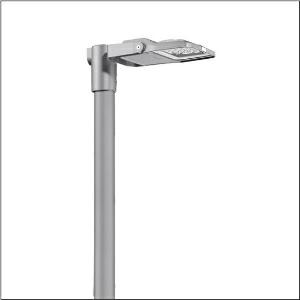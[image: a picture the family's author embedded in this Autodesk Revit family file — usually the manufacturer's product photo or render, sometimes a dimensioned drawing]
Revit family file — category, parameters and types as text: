
# Revit family: floodlight_fl_21_iq_micro___pl61_5xa7762a2c3a_d37b
name_source: partatom
category: Lighting Fixtures
units: mm (PartAtom-declared; Revit-internal decimal feet)

## family parameters
Cut with Voids When Loaded = No
Host = Face
Light Source = No
Part Type = Normal
Room Calculation Point = No
Round Connector Dimension = Use Diameter
Shared = No

## types (1)
- --- (1 x LED, 2910 lm, 23.1 W, 3000K)
    Apparent Load = 23 VA
    CIE Flux Codes = 33 65 98 100 100
    Color Rendering = 70
    Color Temperature = 3000K
    Default Elevation = 1800 mm
    Description = Floodlight FL 21 iQ micro, floodlight, primary light control with lens, of PMMA, primary optical cover: protective disc, of toughened safety glass, transparent, light distribution: PL61, light emission: direct distribution, installation type: surface-mounted, LED, High Power LED, rated luminous flux: 2.910lm, luminous efficacy: 126lm/W, light colour: 730, colour temperature: 3000K, control: Auto-Match, Temp-Guard, Night-Set, Smart-Wire, Desk-Remote (wireless, voltage-free reading and setting of iQ features in the workshop via application-optimized NFC function/RFID function), optimised constant luminous flux control (CLO 2.0), Street-Remote, with terminal, 6-pole, mains connection: 220..240V, AC, 50/60Hz, start of lifetime: 23W, end of service life: 24W, reduction: 11W, luminaire housing, of diecast aluminium, powder-coated, Siteco® metallic grey (DB 702S), corrosivity category C5 mid according to DIN EN ISO 12944, sealing non-destructively replaceable, please order mast flange separately, mast bracket, of steel, galvanised, powder-coated, Siteco® metallic grey (DB 702S), protection rating (complete): IP66, insulation class (complete): insulation class II (safety insulation), certification: CE, ENEC, VDE, protection symbol: D, impact resistance: IK07, permissible operating ambient temperature: -40..+40°C, permissible operating ambient temperature for outdoor applications: -40..+50°C, standard: DIN EN 12944, LABS conformity tested according to VDMA 24364:2018-05, packaging unit: 1 piece

Light Distribution: PL61
    Height = 65 mm
    Lamp = 1 x LED
    Lamp Light Flux = 2910 lm
    Lamp Power = 23.1 W
    Lamp count = 1
    Length = 312 mm
    Luminous efficacy = 126 lm/W
    Manufacturer = Siteco
    ModVariant = No
    Model = 5XA7762A2C3A
    Number of Poles = 1
    OnlyDefault = Yes
    Power Factor = 1
    Product Name = Floodlight FL 21 iQ micro | PL61
    Product group = floodlight | pylon annexe
    ProductGroupID = 6200
    Protection Class = Protection class II
    Protection Degree = IP 66
    RLX_Detail_Level = 1
    RLX_Emergency_Light_Flux = 0 lm
    RLX_Emergency_Type = 0
    RLX_Emergency_Type_DB = No
    RlxData = <blob elided: 101885 chars, md5=f992ae2a>
    Socket = socket
    Standby Power = 0 W
    System Light Flux = 2910 lm
    System Power = 23 W
    Type Comments = factory setting: luminous flux: 100 % | dim-lin: 254 | 455 mA
    Type Image = l_1007121.jpg
    URL = http://relux.com
    VarID = @adj_167053
    Voltage = 0 V
    Weight = 0.00 kg
    Width = 230 mm

## geometry (parser evidence)
native form markers: Blend x4, Sweep x13
no freeform markers — native parametric forms only
